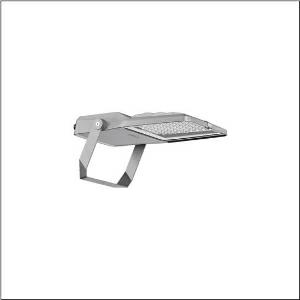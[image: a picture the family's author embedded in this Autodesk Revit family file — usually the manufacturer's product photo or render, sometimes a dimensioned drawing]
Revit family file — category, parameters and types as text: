
# Revit family: floodlight_fl_21_iq_mini___pl64_5xa7772d2e1a_f3f3
name_source: partatom
category: Lighting Fixtures
units: mm (PartAtom-declared; Revit-internal decimal feet)

## family parameters
Cut with Voids When Loaded = No
Host = Face
Light Source = No
Part Type = Normal
Room Calculation Point = No
Round Connector Dimension = Use Diameter
Shared = No

## types (1)
- --- (1 x LED, 17220 lm, 143 W, 3000K)
    Apparent Load = 143 VA
    CIE Flux Codes = 28 80 98 100 100
    Color Rendering = 70
    Color Temperature = 3000K
    Default Elevation = 1800 mm
    Description = Floodlight FL 21 iQ mini, floodlight, primary light control with lens, of PMMA, primary optical cover: protective disc, of toughened safety glass, transparent, light distribution: PL64, light emission: direct distribution, installation type: surface-mounted, LED, High Power LED, rated luminous flux: 17.220lm, luminous efficacy: 120lm/W, light colour: 730, colour temperature: 3000K, control gear: iQ Street-Remote/DALI, control: Street-Remote, Auto-Match, Temp-Guard, Night-Set, Smart-Wire, Desk-Remote (wireless, voltage-free reading and setting of iQ features in the workshop via application-optimized NFC function/RFID function), optimised constant luminous flux control (CLO 2.0), with terminal, 6-pole, mains connection: 220..240V, AC, 50/60Hz, start of lifetime: 143W, end of service life: 152W, reduction: 61W, luminaire housing, of diecast aluminium, powder-coated, Siteco® metallic grey (DB 702S), corrosivity category C5 mid according to DIN EN ISO 12944, suitable for swimming pools, chlorine-resistant, sealing non-destructively replaceable, mounting bracket, of steel, galvanised, powder-coated, Siteco® metallic grey (DB 702S), protection rating (complete): IP66, insulation class (complete): insulation class II (safety insulation), certification: CE, ENEC, VDE, protection symbol: D, impact resistance: IK08, permissible operating ambient temperature: -40..+40°C, permissible operating ambient temperature for outdoor applications: -40..+50°C, standard: DIN EN 12944, LABS conformity tested according to VDMA 24364:2018-05, packaging unit: 1 piece

Light Distribution: PL64
    Height = 70 mm
    Lamp = 1 x LED
    Lamp Light Flux = 17220 lm
    Lamp Power = 143 W
    Lamp count = 1
    Length = 485 mm
    Luminous efficacy = 120 lm/W
    Manufacturer = Siteco
    ModVariant = No
    Model = 5XA7772D2E1A
    Number of Poles = 1
    OnlyDefault = Yes
    Power Factor = 1
    Product Name = Floodlight FL 21 iQ mini | PL64
    Product group = floodlight | pylon annexe
    ProductGroupID = 6200
    Protection Class = Protection class II
    Protection Degree = IP 66
    RLX_Detail_Level = 1
    RLX_Emergency_Light_Flux = 0 lm
    RLX_Emergency_Type = 0
    RLX_Emergency_Type_DB = No
    RlxData = <blob elided: 96497 chars, md5=1556d668>
    Socket = socket
    Standby Power = 0 W
    System Light Flux = 17220 lm
    System Power = 143 W
    Type Comments = factory setting: luminous flux: 100 % | dim-lin: 254 | 730 mA
    Type Image = l_1006845.jpg
    URL = http://relux.com
    VarID = @adj_165878
    Voltage = 0 V
    Weight = 0.00 kg
    Width = 337 mm

## geometry (parser evidence)
native form markers: Blend x4, Sweep x11
no freeform markers — native parametric forms only
